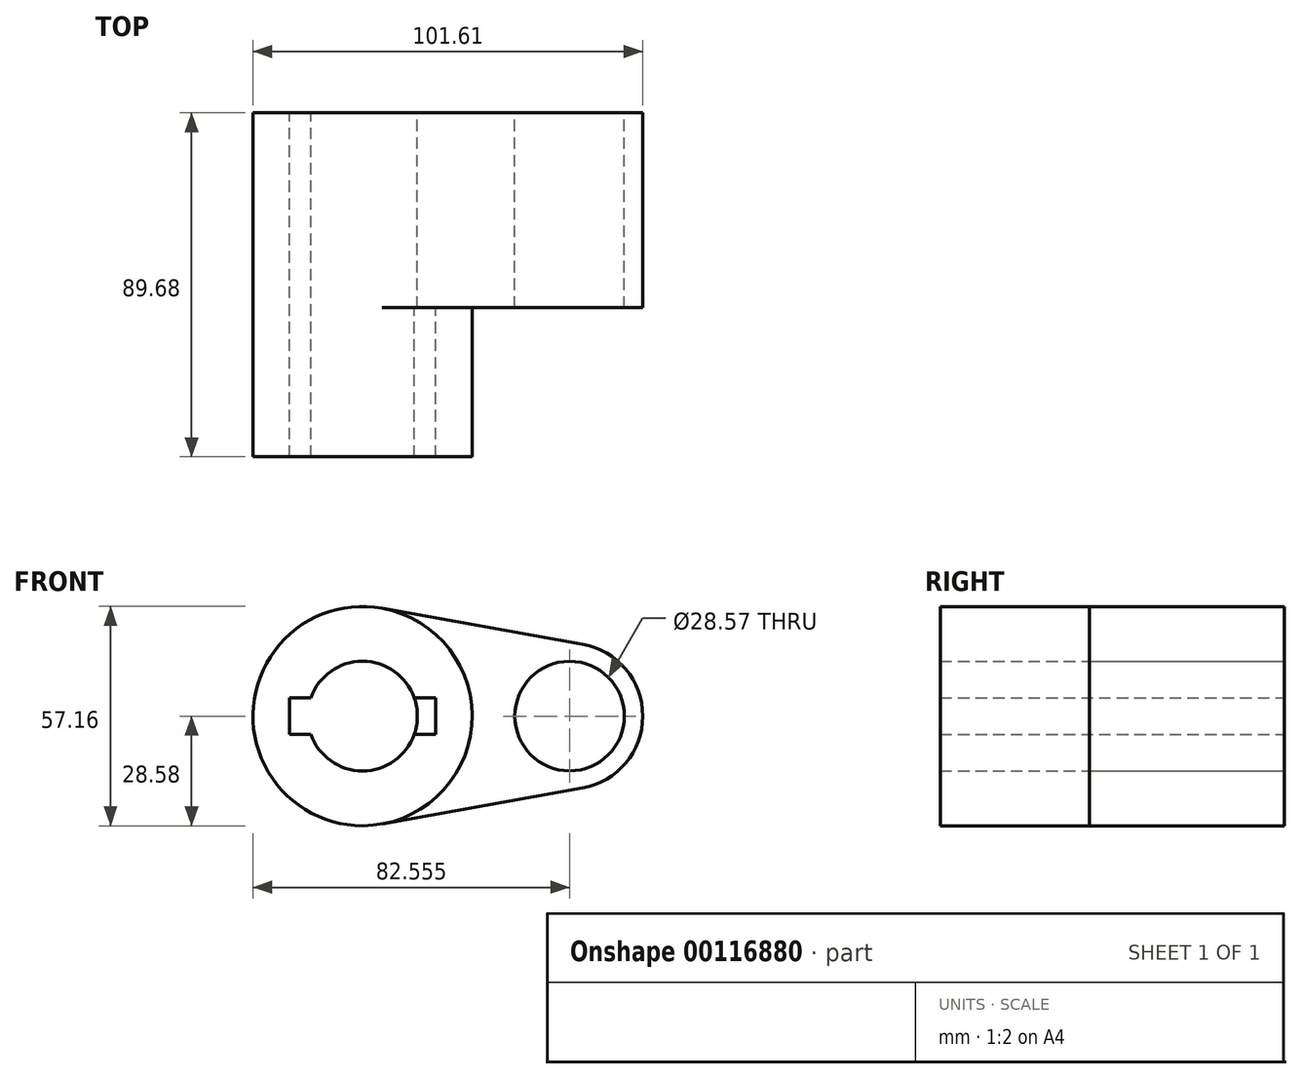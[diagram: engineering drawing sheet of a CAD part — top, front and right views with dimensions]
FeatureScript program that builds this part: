
annotation { "Feature Type Name" : "Feature", "Feature Type Description" : "" }
export const myFeature = defineFeature(function(context is Context, id is Id, definition is map)
    precondition{}
    {
        {
            var Q0;
            Q0=qCreatedBy(makeId("Front.planeOp"),FACE);
            var sketch = newSketch(context, id + "F0", { "sketchPlane" : qUnion([Q0])});
            skSolve(sketch);
        }
        {
            var Q0;
            Q0=qCreatedBy(makeId("Front.planeOp"),FACE);
            var sketch = newSketch(context, id + "F1", { "sketchPlane" : qUnion([Q0])});
            skCircle(sketch, "E0", {"center": v(0, 0) * mm, "radius": 28.58 * mm});
            skCircle(sketch, "E1", {"center": v(53.98, 0) * mm, "radius": 19.05 * mm});
            skLineSegment(sketch, "E2", {"start": v(5.04, 28.13) * mm, "end": v(57.34, 18.75) * mm});
            skLineSegment(sketch, "E3", {"start": v(5.04, -28.13) * mm, "end": v(57.34, -18.75) * mm});
            skCircle(sketch, "E4", {"center": v(0, 0) * mm, "radius": 14.29 * mm});
            skCircle(sketch, "E5", {"center": v(53.98, 0) * mm, "radius": 14.29 * mm});
            skLineSegment(sketch, "E6.bottom", {"start": v(19.05, -4.76) * mm, "end": v(-19.05, -4.76) * mm});
            skLineSegment(sketch, "E6.top", {"start": v(19.05, 4.76) * mm, "end": v(-19.05, 4.76) * mm});
            skLineSegment(sketch, "E6.left", {"start": v(19.05, -4.76) * mm, "end": v(19.05, 4.76) * mm});
            skLineSegment(sketch, "E6.right", {"start": v(-19.05, -4.76) * mm, "end": v(-19.05, 4.76) * mm});
            skSolve(sketch);
        }
        {
            var Q0;
            {var subQ11=sQuery(id+"F1.wireOp",EDGE,"E6.left");Q0=makeQuery(id+"F1.imprint","IMPRINT",FACE,{"disambiguationData":[TD([[makeQuery(id+"F1.imprint","IMPRINT",EDGE,{"derivedFrom":subQ11}),-1.0]])]});}
            var Q1;
            {var subQ0=sQuery(id+"F1.wireOp",EDGE,"E2");Q1=makeQuery(id+"F1.imprint","IMPRINT",FACE,{"disambiguationData":[TD([[makeQuery(id+"F1.imprint","IMPRINT",EDGE,{"derivedFrom":subQ0}),-1.0]])]});}
            var Q2;
            Q2=makeQuery(id+"F1.imprint","IMPRINT",FACE,{"disambiguationData":[TD([[makeQuery(id+"F1.imprint","IMPRINT",EDGE,{"derivedFrom":sQuery(id+"F1.wireOp",EDGE,"E5")}),-1.0]])]});
            var Q3;
            {var subQ5=sQuery(id+"F1.wireOp",EDGE,"E6.left");Q3=makeQuery(id+"F1.imprint","IMPRINT",FACE,{"disambiguationData":[TD([[makeQuery(id+"F1.imprint","IMPRINT",EDGE,{"derivedFrom":subQ5}),1.0]])]});}
            extrude(context, id + "F2", {"entities" : qUnion([Q0, Q1, Q2, Q3]), "depth" : 50.8 * mm});
        }
        {
            var Q0;
            Q0 = qSketchRegion(id + "F0", true);
            var Q1;
            {var subQ11=sQuery(id+"F1.wireOp",EDGE,"E6.left");Q1=makeQuery(id+"F1.imprint","IMPRINT",FACE,{"disambiguationData":[TD([[makeQuery(id+"F1.imprint","IMPRINT",EDGE,{"derivedFrom":subQ11}),-1.0]])]});}
            extrude(context, id + "F3", {"entities" : qUnion([Q0, Q1]), "operationType" : NewBodyOperationType.ADD, "depth" : 89.68 * mm});
        }
    });
